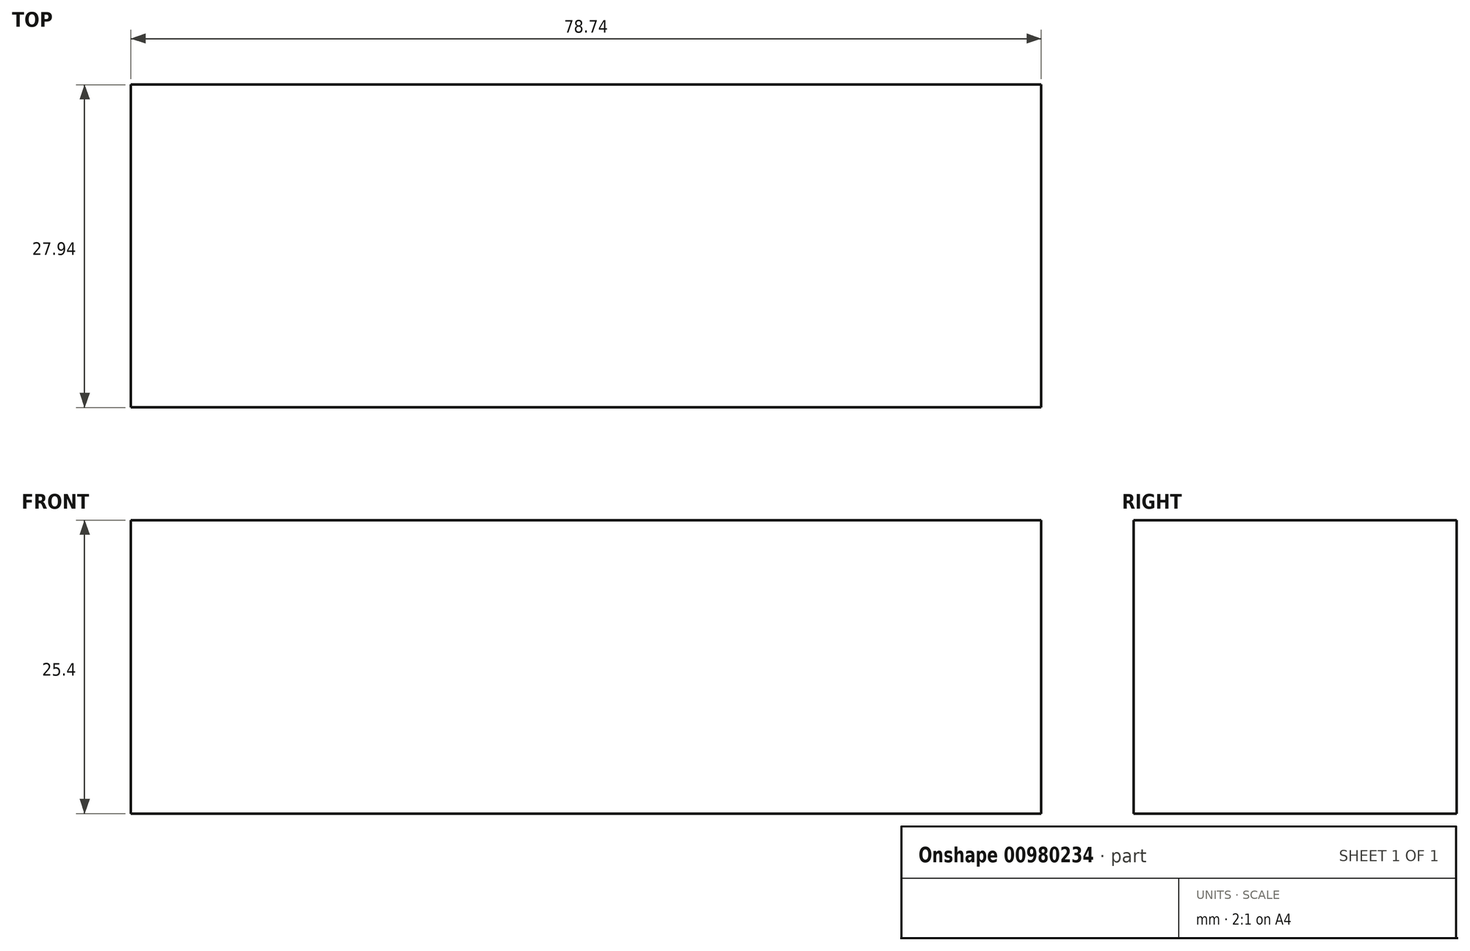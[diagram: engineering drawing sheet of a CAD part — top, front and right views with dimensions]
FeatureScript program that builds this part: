
annotation { "Feature Type Name" : "Feature", "Feature Type Description" : "" }
export const myFeature = defineFeature(function(context is Context, id is Id, definition is map)
    precondition{}
    {
        {
            var Q0;
            Q0=qCreatedBy(makeId("Top.planeOp"),FACE);
            var sketch = newSketch(context, id + "F0", { "sketchPlane" : qUnion([Q0])});
            skLineSegment(sketch, "E0.bottom", {"start": v(-34.26, -6.2) * mm, "end": v(44.48, -6.2) * mm});
            skLineSegment(sketch, "E0.top", {"start": v(-34.26, -34.15) * mm, "end": v(44.48, -34.15) * mm});
            skLineSegment(sketch, "E0.left", {"start": v(-34.26, -6.2) * mm, "end": v(-34.26, -34.15) * mm});
            skLineSegment(sketch, "E0.right", {"start": v(44.48, -6.2) * mm, "end": v(44.48, -34.15) * mm});
            skSolve(sketch);
        }
        {
            var Q0;
            Q0=makeQuery(id+"F0.imprint","IMPRINT",FACE,{"disambiguationData":[TD([[makeQuery(id+"F0.imprint","IMPRINT",EDGE,{"derivedFrom":sQuery(id+"F0.wireOp",EDGE,"E0.bottom")}),-1.0]])]});
            extrude(context, id + "F1", {"entities" : qUnion([Q0]), "depth" : 25.4 * mm, "offsetDistance" : 25.4 * mm});
        }
        {
            var Q0;
            Q0=makeQuery(id+"F1.opExtrude","CAP_FACE",FACE,{"disambiguationData":[OSD([sQuery(id+"F0.wireOp",EDGE,"E0.bottom"),sQuery(id+"F0.wireOp",EDGE,"E0.top"),sQuery(id+"F0.wireOp",EDGE,"E0.left"),sQuery(id+"F0.wireOp",EDGE,"E0.right")])],"isStart":false});
            var sketch = newSketch(context, id + "F2", { "sketchPlane" : qUnion([Q0])});
            skLineSegment(sketch, "E1.bottom", {"start": v(-21.37, -14.82) * mm, "end": v(-31.27, -14.82) * mm});
            skLineSegment(sketch, "E1.top", {"start": v(-21.37, -7.27) * mm, "end": v(-31.27, -7.27) * mm});
            skLineSegment(sketch, "E1.left", {"start": v(-21.37, -14.82) * mm, "end": v(-21.37, -7.27) * mm});
            skLineSegment(sketch, "E1.right", {"start": v(-31.27, -14.82) * mm, "end": v(-31.27, -7.27) * mm});
            skPoint(sketch, "E1.middle", {"position": v(-26.32, -11.04) * mm});
            skSolve(sketch);
        }
    });
